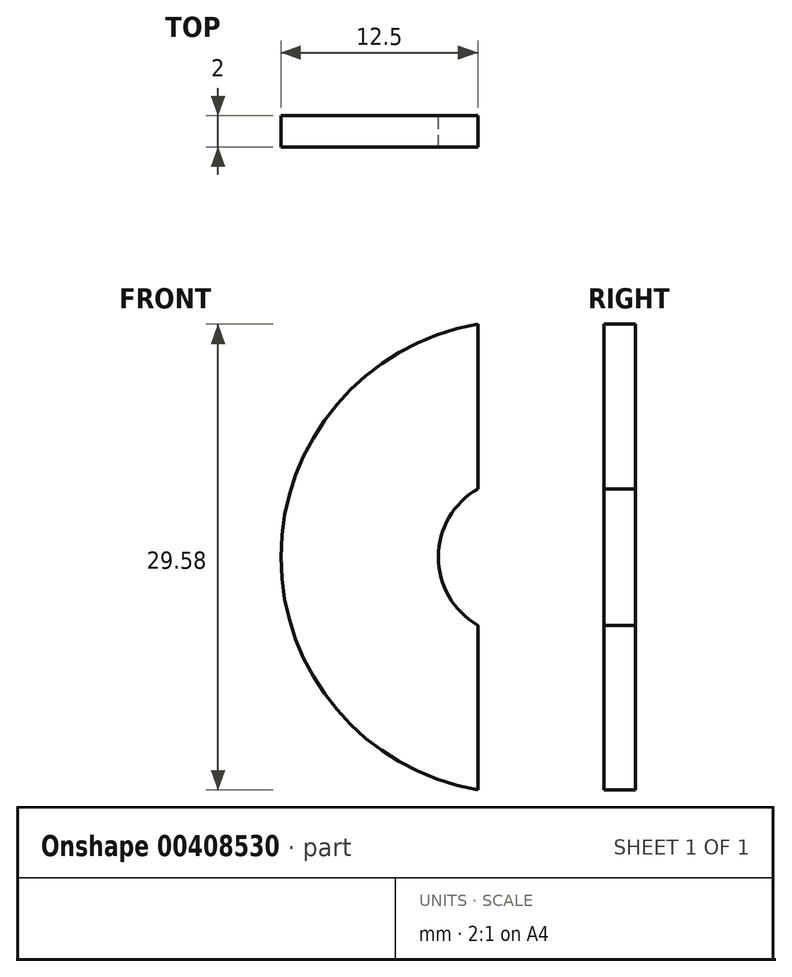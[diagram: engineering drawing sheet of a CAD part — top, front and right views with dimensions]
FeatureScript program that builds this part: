
annotation { "Feature Type Name" : "Feature", "Feature Type Description" : "" }
export const myFeature = defineFeature(function(context is Context, id is Id, definition is map)
    precondition{}
    {
        {
            var Q0;
            Q0=qCreatedBy(makeId("Front.planeOp"),FACE);
            var sketch = newSketch(context, id + "F0", { "sketchPlane" : qUnion([Q0])});
            skLineSegment(sketch, "E0", {"start": v(-2.5, 14.8) * mm, "end": v(-2.5, 4.33) * mm});
            skArc(sketch, "E1", {"start": v(-2.5, 14.8) * mm, "mid": v(-15, 0) * mm, "end": v(-2.5, -14.8) * mm});
            skArc(sketch, "E2", {"start": v(-2.5, -14.8) * mm, "mid": v(15, 0) * mm, "end": v(-2.5, 14.8) * mm, "construction": true});
            skArc(sketch, "E3", {"start": v(-2.5, -4.33) * mm, "mid": v(5, 0) * mm, "end": v(-2.5, 4.33) * mm, "construction": true});
            skArc(sketch, "E4", {"start": v(-2.5, 4.33) * mm, "mid": v(-5, 0) * mm, "end": v(-2.5, -4.33) * mm});
            skLineSegment(sketch, "E5", {"start": v(-2.5, 4.33) * mm, "end": v(-2.5, -4.33) * mm, "construction": true});
            skLineSegment(sketch, "E6", {"start": v(-2.5, -4.33) * mm, "end": v(-2.5, -14.8) * mm});
            skSolve(sketch);
        }
        {
            var Q0;
            Q0 = qSketchRegion(id + "F0", true);
            extrude(context, id + "F1", {"entities" : qUnion([Q0]), "depth" : 2 * mm});
        }
    });
